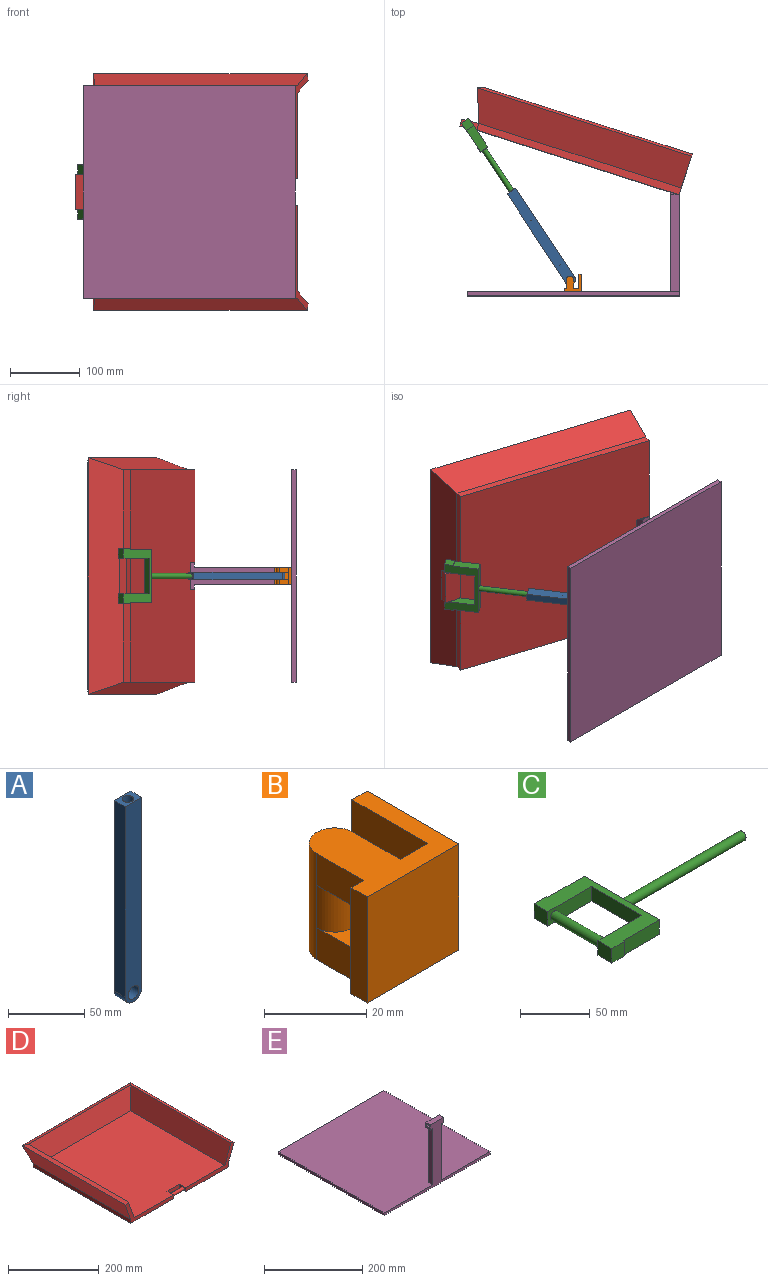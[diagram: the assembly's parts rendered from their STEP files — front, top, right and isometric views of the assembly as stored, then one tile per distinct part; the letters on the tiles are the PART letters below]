
ASSEMBLY  parts=5 mates=5
PART A: 9 faces, bbox 15.2x10.2x160 mm
  f0: cylinder r=7.62mm len=15.24mm, axis (0,1,0), area 243.2mm2, adj f1,f4,f5,f6
  f1: plane 152.4x10.16mm, normal (1,0,0), area 1548.4mm2, adj f0,f2,f5,f6
  f2: plane 15.24x10.16mm, normal (0,0,1), area 109.2mm2, adj f1,f4,f5,f6,f7
  f3: cylinder r=5.08mm len=10.16mm, axis (0,1,0), area 324.3mm2, adj f5,f6
  f4: plane 152.4x10.16mm, normal (-1,0,0), area 1548.4mm2, adj f0,f2,f5,f6
  f5: plane 160.02x15.24mm, normal (0,-1,0), area 2332.7mm2, adj f0,f1,f2,f3,f4
  f6: plane 160.02x15.24mm, normal (0,1,0), area 2332.7mm2, adj f0,f1,f2,f3,f4
  f7: cylinder r=3.81mm len=127mm, axis (0,0,1), area 3040.2mm2, adj f2,f8
  f8: plane 7.62x7.62mm, normal (0,0,1), area 45.6mm2, adj f7
PART B: 15 faces, bbox 25.4x25.4x25.4 mm
  f0: plane 25.4x25.4mm, normal (0,0,1), area 373.2mm2, adj f2,f3,f4,f5,f6,f7,f8,f9
  f1: plane 25.4x25.4mm, normal (0,0,-1), area 373.2mm2, adj f2,f3,f4,f5,f6,f7,f8,f9
  f2: plane 25.4x25.4mm, normal (0,-1,0), area 645.2mm2, adj f0,f1,f3,f5
  f3: plane 25.4x25.4mm, normal (1,0,0), area 645.2mm2, adj f0,f1,f2,f4
  f4: plane 25.4x4.2mm, normal (0,1,0), area 106.7mm2, adj f0,f1,f3,f8
  f5: plane 25.4x4.46mm, normal (-1,0,0), area 113.2mm2, adj f0,f1,f2,f6
  f6: plane 25.4x21.2mm, normal (0,1,0), area 383.6mm2, adj f0,f1,f5,f7,f8,f9,f10,f12
  f7: plane 25.4x12.9mm, normal (1,0,0), area 196.9mm2, adj f0,f1,f6,f10,f11,f12,f13
  f8: plane 25.4x20.94mm, normal (-1,0,0), area 531.9mm2, adj f0,f1,f4,f6
  f9: plane 25.4x12.99mm, normal (-1,0,0), area 199.1mm2, adj f0,f1,f6,f10,f12,f13,f14
  f10: plane 12.89x10.16mm, normal (0,0,-1), area 90.9mm2, adj f6,f7,f9,f11,f14
  f11: plane 10.16x0mm, normal (0,-1,0), area 0mm2, adj f7,f10,f12,f14
  f12: plane 12.89x10.16mm, normal (0,0,1), area 90.9mm2, adj f6,f7,f9,f11,f14
  f13: cylinder r=5.08mm len=25.4mm, axis (0,0,1), area 404.9mm2, adj f0,f1,f7,f9
  f14: cylinder r=5.08mm len=10.16mm, axis (0,0,1), area 161mm2, adj f9,f10,f11,f12
PART C: 17 faces, bbox 171.5x78.7x12.7 mm
  f0: cylinder r=3.81mm len=50.8mm, axis (0,1,0), area 1216.1mm2, adj f6,f10
  f1: plane 78.74x49.53mm, normal (0,0,-1), area 1548.4mm2, adj f2,f4,f5,f6,f7,f8,f9,f10
  f2: plane 12.7x1.27mm, normal (1,0,0), area 16.1mm2, adj f1,f3,f5,f11
  f3: plane 78.74x49.53mm, normal (0,0,1), area 1548.4mm2, adj f2,f4,f5,f6,f7,f8,f9,f10
  f4: plane 13.97x12.7mm, normal (-1,0,0), area 177.4mm2, adj f1,f3,f5,f6
  f5: plane 12.7x12.7mm, normal (0,-1,0), area 161.3mm2, adj f1,f2,f3,f4
  f6: plane 44.45x12.7mm, normal (0,1,0), area 518.9mm2, adj f0,f1,f3,f4,f13
  f7: plane 13.97x12.7mm, normal (-1,0,0), area 177.4mm2, adj f1,f3,f9,f10
  f8: plane 12.7x1.27mm, normal (1,0,0), area 16.1mm2, adj f1,f3,f9,f16
  f9: plane 12.7x12.7mm, normal (0,1,0), area 161.3mm2, adj f1,f3,f7,f8
  f10: plane 44.45x12.7mm, normal (0,-1,0), area 518.9mm2, adj f0,f1,f3,f7,f13
  f11: plane 36.83x12.7mm, normal (0,-1,0), area 467.7mm2, adj f1,f2,f3,f12
  f12: plane 76.2x12.7mm, normal (1,0,0), area 922.1mm2, adj f1,f3,f11,f14,f16
  f13: plane 50.8x12.7mm, normal (-1,0,0), area 645.2mm2, adj f1,f3,f6,f10
  f14: cylinder r=3.81mm len=121.92mm, axis (-1,0,0), area 2918.6mm2, adj f12,f15
  f15: plane 7.62x7.62mm, normal (1,0,0), area 45.6mm2, adj f14
  f16: plane 36.83x12.7mm, normal (0,1,0), area 467.7mm2, adj f1,f3,f8,f12
PART D: 27 faces, bbox 339.5x330.1x63.1 mm
  f0: plane 293.99x283.18mm, normal (0,0,1), area 82476.1mm2, adj f1,f7,f8,f9,f15,f23,f24,f25
  f1: plane 150.72x61.37mm, normal (0,-1,0), area 1889.7mm2, adj f0,f5,f6,f8,f10,f12,f23
  f2: plane 127x10.16mm, normal (0,1,-0.07), area 1293.4mm2, adj f11,f12,f14,f18
  f3: plane 322.17x47.74mm, normal (-0.94,0,-0.34), area 15925.2mm2, adj f4,f9,f11,f14
  f4: plane 322.17x9.55mm, normal (-0.34,0,0.94), area 3224.8mm2, adj f3,f7,f9,f13
  f5: plane 322.17x9.55mm, normal (0.34,0,0.94), area 3224.8mm2, adj f1,f6,f8,f13
  f6: plane 322.17x47.74mm, normal (0.94,0,-0.34), area 15925.2mm2, adj f1,f5,f10,f14
  f7: plane 312.63x51.21mm, normal (0.94,0,0.34), area 16529.6mm2, adj f0,f4,f9,f15
  f8: plane 312.63x51.21mm, normal (-0.94,0,0.34), area 16529.6mm2, adj f0,f1,f5,f15
  f9: plane 150.72x61.37mm, normal (0,-1,0), area 1889.7mm2, adj f0,f3,f4,f7,f11,f12,f24
  f10: plane 304.8x10.16mm, normal (1,0,0), area 3093.2mm2, adj f1,f6,f12,f16
  f11: plane 304.8x10.16mm, normal (-1,0,0), area 3093.2mm2, adj f2,f3,f9,f12
  f12: plane 304.8x304.1mm, normal (0,0,-1), area 91915.6mm2, adj f1,f2,f9,f10,f11,f16,f17,f23
  f13: plane 339.55x9.55mm, normal (0,0.34,0.94), area 3352.8mm2, adj f4,f5,f14,f15
  f14: plane 339.55x47.74mm, normal (0,0.94,-0.34), area 16366.5mm2, adj f2,f3,f6,f13,f16,f19
  f15: plane 320.45x51.21mm, normal (0,-0.94,0.34), area 16448.3mm2, adj f0,f7,f8,f13
  f16: plane 127x10.16mm, normal (0,1,-0.07), area 1293.4mm2, adj f10,f12,f14,f20
  f17: plane 50.8x25.34mm, normal (0,-0.07,-1), area 1290.3mm2, adj f12,f18,f20,f21
  f18: plane 26.04x11.91mm, normal (-1,0,0), area 213.1mm2, adj f2,f17,f19,f21,f22
  f19: plane 50.8x25.34mm, normal (0,0.07,1), area 1290.3mm2, adj f14,f18,f20,f21
  f20: plane 26.04x11.91mm, normal (1,0,0), area 213.1mm2, adj f16,f17,f19,f21,f22
  f21: plane 50.8x10.16mm, normal (0,1,-0.07), area 517.4mm2, adj f17,f18,f19,f20
  f22: cylinder r=3.81mm len=50.8mm, axis (-1,0,0), area 1216.1mm2, adj f18,f20
  f23: plane 20.32x10.16mm, normal (-1,0,0), area 160.8mm2, adj f0,f1,f12,f25,f26
  f24: plane 20.32x10.16mm, normal (1,0,0), area 160.8mm2, adj f0,f9,f12,f25,f26
  f25: plane 38.1x10.16mm, normal (0,-1,0), area 387.1mm2, adj f0,f12,f23,f24
  f26: cylinder r=3.81mm len=38.1mm, axis (1,0,0), area 912.1mm2, adj f23,f24
PART E: 15 faces, bbox 304.8x304.8x158.8 mm
  f0: plane 304.8x304.8mm, normal (0,0,1), area 92580.5mm2, adj f1,f2,f3,f4,f6,f7,f8
  f1: plane 304.8x158.75mm, normal (0,-1,0), area 5967.7mm2, adj f0,f2,f4,f5,f6,f8,f9,f10
  f2: plane 304.8x6.35mm, normal (1,0,0), area 1935.5mm2, adj f0,f1,f3,f5
  f3: plane 304.8x6.35mm, normal (0,1,0), area 1935.5mm2, adj f0,f2,f4,f5
  f4: plane 304.8x6.35mm, normal (-1,0,0), area 1935.5mm2, adj f0,f1,f3,f5
  f5: plane 304.8x304.8mm, normal (0,0,-1), area 92903mm2, adj f1,f2,f3,f4
  f6: plane 139.7x12.7mm, normal (1,0,0), area 1774.2mm2, adj f0,f1,f7,f9
  f7: plane 152.4x38.1mm, normal (0,1,0), area 4032.3mm2, adj f0,f6,f8,f9,f10,f11,f12,f13
  f8: plane 139.7x12.7mm, normal (-1,0,0), area 1774.2mm2, adj f0,f1,f7,f13
  f9: plane 12.7x6.35mm, normal (0,0,-1), area 80.6mm2, adj f1,f6,f7,f10
  f10: plane 12.7x12.7mm, normal (1,0,0), area 115.7mm2, adj f1,f7,f9,f12,f14
  f11: plane 12.7x12.7mm, normal (-1,0,0), area 115.7mm2, adj f1,f7,f12,f13,f14
  f12: plane 38.1x12.7mm, normal (0,0,1), area 483.9mm2, adj f1,f7,f10,f11
  f13: plane 12.7x6.35mm, normal (0,0,-1), area 80.6mm2, adj f1,f7,f8,f11
  f14: cylinder r=3.81mm len=38.1mm, axis (1,0,0), area 912.1mm2, adj f10,f11
PLACE A rot(axis=(-0.92,-0.28,0.28),94.7deg) t=(81.51,181.01,-130.59)mm
PLACE B t=(85.67,176.31,-138.21)mm fixed
PLACE C rot(axis=(0.8,-0.43,-0.43),103deg) t=(-65.31,403.66,-125.51)mm
PLACE D rot(axis=(-0.51,0.7,0.51),110.4deg) t=(237.94,302.5,-277.91)mm
PLACE E rot(axis=(-0.58,0.58,0.58),120deg) t=(238.58,157.26,-277.91)mm
MATE revolute D.f22 <-> C.f0  axis (0,0,-1) through (-65.31,403.66,-150.91)mm
MATE revolute E.f14 <-> D.f26  axis (0,0,-1) through (232.23,309.66,-144.56)mm
MATE fastened E.f0 <-> B.f2  axis (0,1,0) through (85.67,163.61,-125.51)mm
MATE revolute A.f3 <-> B.f13  axis (0,0,-1) through (81.51,181.01,-130.59)mm
MATE slider C.f14 <-> A.f7  axis (0.55,-0.83,0) through (25.58,265.83,-125.51)mm
